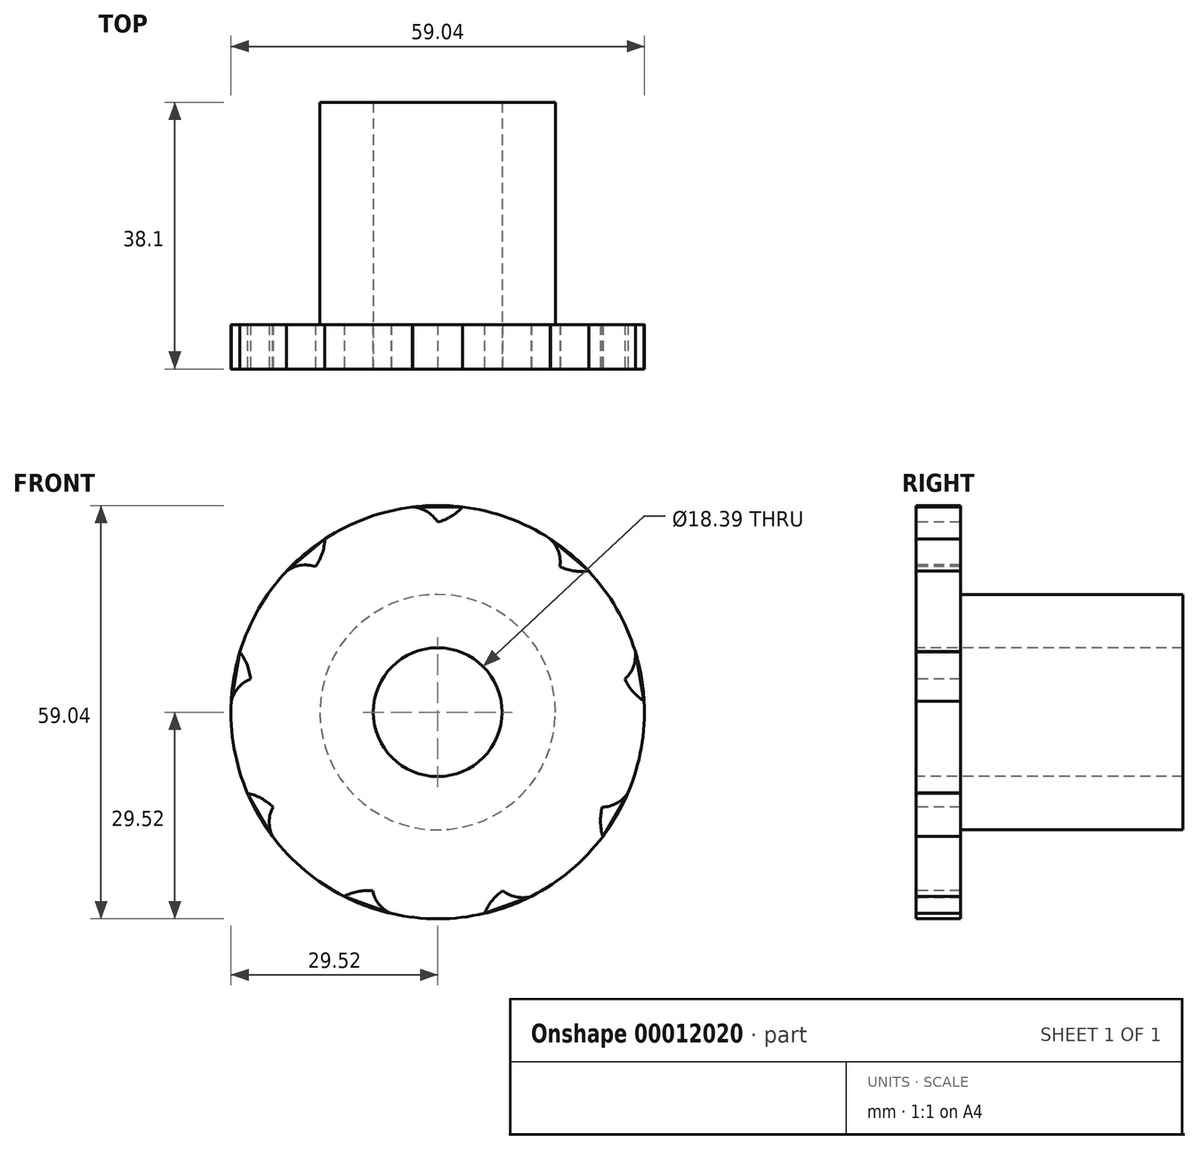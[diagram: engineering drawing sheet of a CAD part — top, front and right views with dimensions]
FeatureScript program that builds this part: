
annotation { "Feature Type Name" : "Feature", "Feature Type Description" : "" }
export const myFeature = defineFeature(function(context is Context, id is Id, definition is map)
    precondition{}
    {
        {
            var Q0;
            Q0=qCreatedBy(makeId("Right.planeOp"),FACE);
            var sketch = newSketch(context, id + "F0", { "sketchPlane" : qUnion([Q0])});
            skLineSegment(sketch, "E0", {"start": v(0, 0) * mm, "end": v(38.1, 0) * mm, "construction": true});
            skLineSegment(sketch, "E1.bottom", {"start": v(0, 29.52) * mm, "end": v(6.35, 29.52) * mm});
            skLineSegment(sketch, "E1.top", {"start": v(0, 16.82) * mm, "end": v(6.35, 16.82) * mm});
            skLineSegment(sketch, "E1.left", {"start": v(0, 29.52) * mm, "end": v(0, 16.82) * mm});
            skLineSegment(sketch, "E1.right", {"start": v(6.35, 29.52) * mm, "end": v(6.35, 16.82) * mm});
            skLineSegment(sketch, "E2.bottom", {"start": v(0, 16.82) * mm, "end": v(38.1, 16.82) * mm});
            skLineSegment(sketch, "E2.top", {"start": v(0, 9.2) * mm, "end": v(38.1, 9.2) * mm});
            skLineSegment(sketch, "E2.left", {"start": v(0, 16.82) * mm, "end": v(0, 9.2) * mm});
            skLineSegment(sketch, "E2.right", {"start": v(38.1, 16.82) * mm, "end": v(38.1, 9.2) * mm});
            skLineSegment(sketch, "E3.0.MirrorCS", {"start": v(0, -9.2) * mm, "end": v(38.1, -9.2) * mm});
            skLineSegment(sketch, "E4.0.MirrorCS", {"start": v(0, -16.82) * mm, "end": v(38.1, -16.82) * mm});
            skLineSegment(sketch, "E5.0.MirrorCS", {"start": v(0, -29.52) * mm, "end": v(6.35, -29.52) * mm});
            skLineSegment(sketch, "E5.1.MirrorCS", {"start": v(0, -16.82) * mm, "end": v(6.35, -16.82) * mm});
            skLineSegment(sketch, "E5.2.MirrorCS", {"start": v(38.1, -16.82) * mm, "end": v(38.1, -9.2) * mm});
            skLineSegment(sketch, "E5.3.MirrorCS", {"start": v(0, -16.82) * mm, "end": v(0, -9.2) * mm});
            skLineSegment(sketch, "E5.5.MirrorCS", {"start": v(0, -29.52) * mm, "end": v(0, -16.82) * mm});
            skLineSegment(sketch, "E5.6.MirrorCS", {"start": v(6.35, -29.52) * mm, "end": v(6.35, -16.82) * mm});
            skSolve(sketch);
        }
        {
            var Q0;
            Q0=makeQuery(id+"F0.imprint","IMPRINT",FACE,{"disambiguationData":[TD([[makeQuery(id+"F0.imprint","IMPRINT",EDGE,{"derivedFrom":sQuery(id+"F0.wireOp",EDGE,"E1.bottom")}),-1.0]])]});
            var Q1;
            Q1=makeQuery(id+"F0.imprint","IMPRINT",FACE,{"disambiguationData":[TD([[makeQuery(id+"F0.imprint","IMPRINT",EDGE,{"derivedFrom":sQuery(id+"F0.wireOp",EDGE,"E2.top")}),1.0]])]});
            var Q2;
            Q2=sQuery(id+"F0.wireOp",EDGE,"E0");
            revolve(context, id + "F1", {"entities" : qUnion([Q0, Q1]), "axis" : qUnion([Q2]), "revolveType" : RevolveType.FULL});
        }
        {
            var Q0;
            Q0=makeQuery(id+"F1.opRevolve","SWEPT_FACE",FACE,{"disambiguationData":[OSD([sQuery(id+"F0.wireOp",EDGE,"E1.left"),sQuery(id+"F0.wireOp",EDGE,"E2.left")])]});
            var sketch = newSketch(context, id + "F2", { "sketchPlane" : qUnion([Q0])});
            skArc(sketch, "E6", {"start": v(0, 27.15) * mm, "mid": v(1.93, 27.97) * mm, "end": v(3.55, 29.3) * mm});
            skArc(sketch, "E7", {"start": v(0, 27.15) * mm, "mid": v(-1.65, 28.73) * mm, "end": v(-3.87, 29.3) * mm});
            skLineSegment(sketch, "E8", {"start": v(3.55, 29.3) * mm, "end": v(-3.83, 29.3) * mm});
            skLineSegment(sketch, "E9", {"start": v(-3.83, 29.3) * mm, "end": v(3.55, 29.3) * mm});
            skArc(sketch, "E10.1.0", {"start": v(17.45, 20.8) * mm, "mid": v(19.46, 20.18) * mm, "end": v(21.56, 20.16) * mm});
            skArc(sketch, "E10.1.1", {"start": v(17.45, 20.8) * mm, "mid": v(17.2, 23.07) * mm, "end": v(15.87, 24.94) * mm});
            skLineSegment(sketch, "E10.1.2", {"start": v(21.56, 20.16) * mm, "end": v(15.9, 24.9) * mm});
            skArc(sketch, "E10.2.0", {"start": v(26.74, 4.71) * mm, "mid": v(27.88, 2.95) * mm, "end": v(29.47, 1.59) * mm});
            skArc(sketch, "E10.2.1", {"start": v(26.74, 4.71) * mm, "mid": v(28, 6.62) * mm, "end": v(28.18, 8.9) * mm});
            skLineSegment(sketch, "E10.2.2", {"start": v(29.47, 1.59) * mm, "end": v(28.2, 8.86) * mm});
            skArc(sketch, "E10.3.0", {"start": v(23.51, -13.57) * mm, "mid": v(23.25, -15.66) * mm, "end": v(23.6, -17.73) * mm});
            skArc(sketch, "E10.3.1", {"start": v(23.51, -13.57) * mm, "mid": v(25.7, -12.93) * mm, "end": v(27.31, -11.3) * mm});
            skLineSegment(sketch, "E10.3.2", {"start": v(23.6, -17.73) * mm, "end": v(27.3, -11.33) * mm});
            skArc(sketch, "E10.4.0", {"start": v(9.29, -25.51) * mm, "mid": v(7.75, -26.94) * mm, "end": v(6.68, -28.75) * mm});
            skArc(sketch, "E10.4.1", {"start": v(9.29, -25.51) * mm, "mid": v(11.38, -26.43) * mm, "end": v(13.66, -26.21) * mm});
            skLineSegment(sketch, "E10.4.2", {"start": v(6.68, -28.75) * mm, "end": v(13.62, -26.22) * mm});
            skArc(sketch, "E10.5.0", {"start": v(-9.29, -25.51) * mm, "mid": v(-11.38, -25.62) * mm, "end": v(-13.36, -26.32) * mm});
            skArc(sketch, "E10.5.1", {"start": v(-9.29, -25.51) * mm, "mid": v(-8.27, -27.57) * mm, "end": v(-6.38, -28.86) * mm});
            skLineSegment(sketch, "E10.5.2", {"start": v(-13.36, -26.32) * mm, "end": v(-6.42, -28.85) * mm});
            skArc(sketch, "E10.6.0", {"start": v(-23.51, -13.57) * mm, "mid": v(-25.19, -12.3) * mm, "end": v(-27.15, -11.57) * mm});
            skArc(sketch, "E10.6.1", {"start": v(-23.51, -13.57) * mm, "mid": v(-24.06, -15.8) * mm, "end": v(-23.44, -18) * mm});
            skLineSegment(sketch, "E10.6.2", {"start": v(-27.15, -11.57) * mm, "end": v(-23.46, -17.97) * mm});
            skArc(sketch, "E10.7.0", {"start": v(-26.74, 4.71) * mm, "mid": v(-27.2, 6.76) * mm, "end": v(-28.24, 8.59) * mm});
            skArc(sketch, "E10.7.1", {"start": v(-26.74, 4.71) * mm, "mid": v(-28.58, 3.36) * mm, "end": v(-29.53, 1.28) * mm});
            skLineSegment(sketch, "E10.7.2", {"start": v(-28.24, 8.59) * mm, "end": v(-29.52, 1.32) * mm});
            skArc(sketch, "E10.8.0", {"start": v(-17.45, 20.8) * mm, "mid": v(-16.5, 22.67) * mm, "end": v(-16.11, 24.73) * mm});
            skArc(sketch, "E10.8.1", {"start": v(-17.45, 20.8) * mm, "mid": v(-19.74, 20.95) * mm, "end": v(-21.8, 19.96) * mm});
            skLineSegment(sketch, "E10.8.2", {"start": v(-16.11, 24.73) * mm, "end": v(-21.77, 19.98) * mm});
            skPoint(sketch, "E10.center", {"position": v(0, 0) * mm});
            skLineSegment(sketch, "E10.anchor1", {"start": v(0, 0) * mm, "end": v(0, 27.15) * mm, "construction": true});
            skLineSegment(sketch, "E10.anchor2", {"start": v(0, 0) * mm, "end": v(-17.45, 20.8) * mm, "construction": true});
            skSolve(sketch);
        }
        {
            var Q0;
            Q0 = qSketchRegion(id + "F2", true);
            extrude(context, id + "F3", {"entities" : qUnion([Q0]), "operationType" : NewBodyOperationType.REMOVE, "oppositeDirection" : true, "depth" : 25.4 * mm, "hasSecondDirection" : true, "secondDirectionOppositeDirection" : false, "secondDirectionDepth" : 25.4 * mm});
        }
    });
